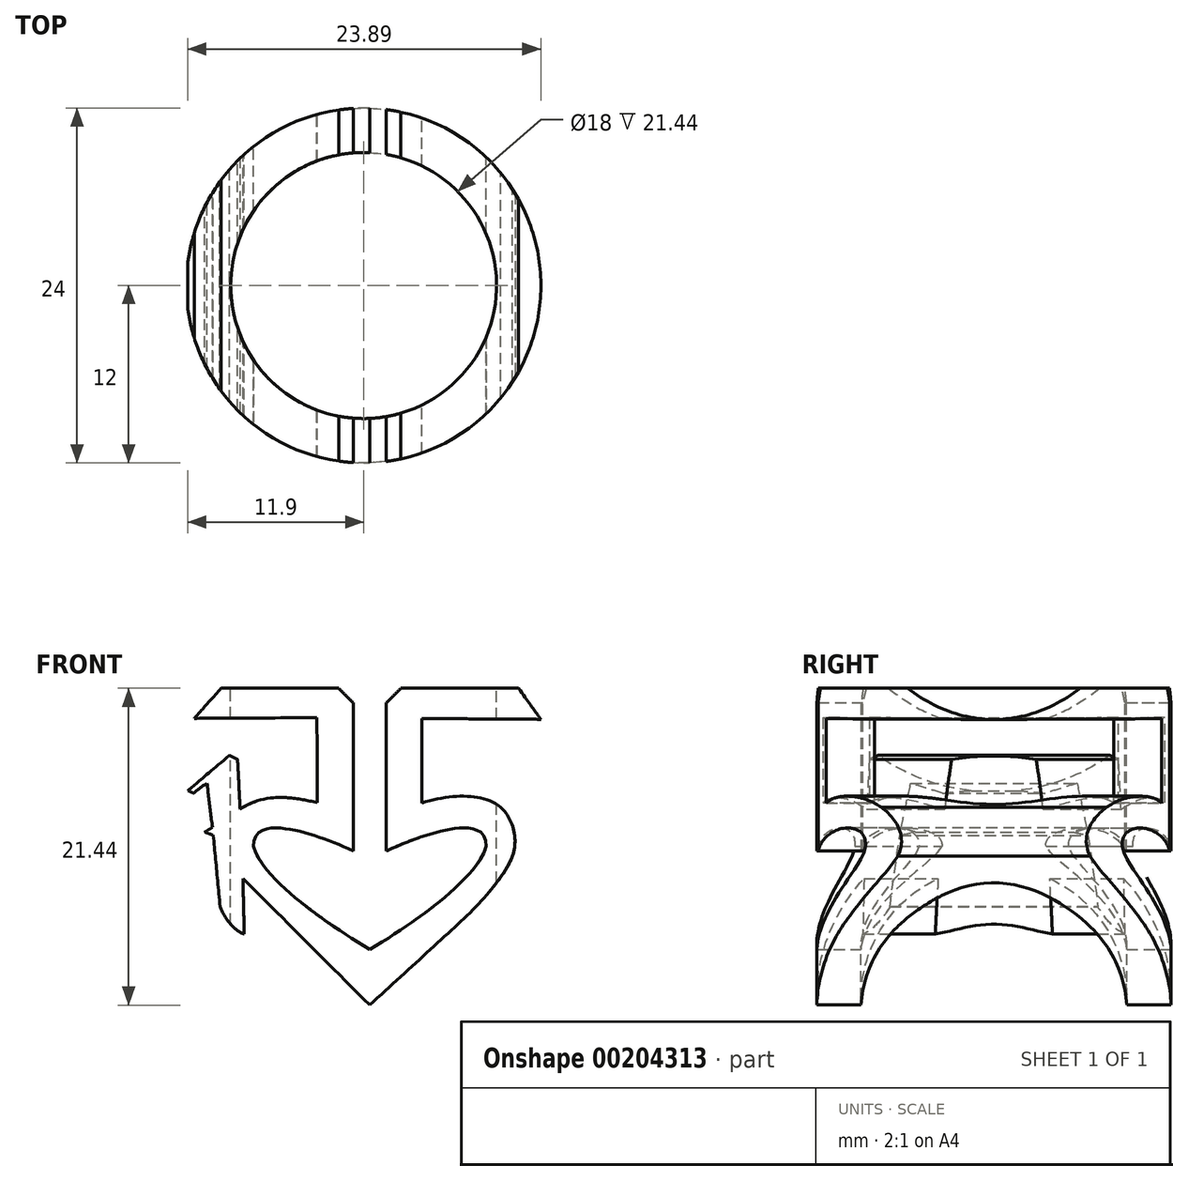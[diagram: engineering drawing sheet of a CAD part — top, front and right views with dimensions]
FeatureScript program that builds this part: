
annotation { "Feature Type Name" : "Feature", "Feature Type Description" : "" }
export const myFeature = defineFeature(function(context is Context, id is Id, definition is map)
    precondition{}
    {
        {
            var Q0;
            Q0=qCreatedBy(makeId("Top.planeOp"),FACE);
            var sketch = newSketch(context, id + "F0", { "sketchPlane" : qUnion([Q0])});
            skCircle(sketch, "E0", {"center": v(0, 0) * mm, "radius": 9 * mm});
            skCircle(sketch, "E1.0", {"center": v(0, 0) * mm, "radius": 12 * mm});
            skPoint(sketch, "E2", {"position": v(-12, 0) * mm});
            skPoint(sketch, "E3", {"position": v(12, 0) * mm});
            skSolve(sketch);
        }
        {
            var Q0;
            Q0=makeQuery(id+"F0.imprint","IMPRINT",FACE,{"disambiguationData":[TD([[makeQuery(id+"F0.imprint","IMPRINT",EDGE,{"derivedFrom":sQuery(id+"F0.wireOp",EDGE,"E0")}),-1.0]])]});
            extrude(context, id + "F1", {"entities" : qUnion([Q0]), "oppositeDirection" : true, "depth" : 26.1 * mm});
        }
        {
            var Q0;
            Q0=qCreatedBy(makeId("Front.planeOp"),FACE);
            var sketch = newSketch(context, id + "F2", { "sketchPlane" : qUnion([Q0])});
            skLineSegment(sketch, "E4.0", {"start": v(-15.68, 5) * mm, "end": v(-15.68, -16.21) * mm});
            skLineSegment(sketch, "E4.1", {"start": v(-15.68, -26.77) * mm, "end": v(15.68, -26.77) * mm});
            skLineSegment(sketch, "E4.2", {"start": v(15.68, -26.77) * mm, "end": v(15.68, -16.21) * mm});
            skLineSegment(sketch, "E4.3", {"start": v(-15.68, -16.21) * mm, "end": v(-15.68, -26.77) * mm});
            skLineSegment(sketch, "E4.4", {"start": v(15.68, 5) * mm, "end": v(15.68, -16.21) * mm});
            skLineSegment(sketch, "E4.5", {"start": v(15.68, 5) * mm, "end": v(-15.68, 5) * mm});
            skLineSegment(sketch, "E5", {"start": v(12, -3.2) * mm, "end": v(10.47, -1.1) * mm});
            skLineSegment(sketch, "E6", {"start": v(10.47, -1.1) * mm, "end": v(2.52, -1.1) * mm});
            skLineSegment(sketch, "E7", {"start": v(2.52, -1.1) * mm, "end": v(1.54, -2.09) * mm});
            skLineSegment(sketch, "E8", {"start": v(1.54, -2.09) * mm, "end": v(1.54, -12.1) * mm});
            skFitSpline(sketch, "E9", {"points": [v(0.42, -18.78) * mm, v(-7.44, -11.8) * mm], "startDerivative": vector(-11.84, 7.14) * mm, "endDerivative": vector(-1.22, 5.47) * mm});
            skFitSpline(sketch, "E10", {"points": [v(-7.44, -11.8) * mm, v(-0.7, -12.1) * mm], "startDerivative": vector(-0.48, 8.4) * mm, "endDerivative": vector(2.37, -1.11) * mm});
            skLineSegment(sketch, "E11", {"start": v(-0.7, -12.1) * mm, "end": v(-0.7, -2.09) * mm});
            skLineSegment(sketch, "E12.MirrorCS", {"start": v(-1.69, -1.1) * mm, "end": v(-0.7, -2.09) * mm});
            skLineSegment(sketch, "E13.MirrorCS", {"start": v(-9.64, -1.1) * mm, "end": v(-1.69, -1.1) * mm});
            skLineSegment(sketch, "E14", {"start": v(-9.64, -1.1) * mm, "end": v(-11.47, -3.14) * mm});
            skLineSegment(sketch, "E15", {"start": v(-11.47, -3.14) * mm, "end": v(-3.16, -3.09) * mm});
            skLineSegment(sketch, "E16", {"start": v(-3.16, -3.09) * mm, "end": v(-3.13, -8.84) * mm});
            skLineSegment(sketch, "E17", {"start": v(12, -3.2) * mm, "end": v(3.93, -3.15) * mm});
            skLineSegment(sketch, "E18", {"start": v(3.93, -3.15) * mm, "end": v(3.93, -8.86) * mm});
            skFitSpline(sketch, "E19", {"points": [v(3.93, -8.86) * mm, v(9.27, -9.16) * mm], "startDerivative": vector(5.06, 1.58) * mm, "endDerivative": vector(3.87, -3.25) * mm});
            skFitSpline(sketch, "E20", {"points": [v(9.27, -9.16) * mm, v(10.08, -12.46) * mm], "startDerivative": vector(2.58, -2.38) * mm, "endDerivative": vector(-1.17, -3.7) * mm});
            skPoint(sketch, "E21", {"position": v(6.16, -17.29) * mm});
            skFitSpline(sketch, "E22", {"points": [v(6.16, -17.27) * mm, v(10.08, -12.46) * mm], "startDerivative": vector(2.98, 2.71) * mm, "endDerivative": vector(2.23, 5.47) * mm});
            skLineSegment(sketch, "E23", {"start": v(6.16, -17.27) * mm, "end": v(0.4, -22.54) * mm});
            skLineSegment(sketch, "E24", {"start": v(0.4, -22.54) * mm, "end": v(-8.17, -13.97) * mm});
            skLineSegment(sketch, "E25", {"start": v(-8.17, -13.97) * mm, "end": v(-8.08, -17.73) * mm});
            skFitSpline(sketch, "E26", {"points": [v(-8.08, -17.73) * mm, v(-9.72, -15.87) * mm], "startDerivative": vector(-3.5, 1.22) * mm, "endDerivative": vector(0.33, -0.8) * mm});
            skLineSegment(sketch, "E27", {"start": v(-9.72, -15.87) * mm, "end": v(-10.18, -11.05) * mm});
            skLineSegment(sketch, "E28", {"start": v(-10.18, -11.05) * mm, "end": v(-10.75, -10.83) * mm});
            skLineSegment(sketch, "E29", {"start": v(-10.75, -10.83) * mm, "end": v(-10.23, -10.51) * mm});
            skLineSegment(sketch, "E30", {"start": v(-10.23, -10.51) * mm, "end": v(-10.6, -7.55) * mm});
            skFitSpline(sketch, "E31", {"points": [v(-10.6, -7.55) * mm, v(-11.48, -8.2) * mm], "startDerivative": vector(-1.38, -0.68) * mm, "endDerivative": vector(-0.49, -0.5) * mm});
            skLineSegment(sketch, "E32", {"start": v(-11.48, -8.2) * mm, "end": v(-11.9, -8.03) * mm});
            skLineSegment(sketch, "E33", {"start": v(-11.9, -8.03) * mm, "end": v(-9.1, -5.64) * mm});
            skLineSegment(sketch, "E34", {"start": v(-9.1, -5.64) * mm, "end": v(-8.53, -5.92) * mm});
            skLineSegment(sketch, "E35", {"start": v(-8.53, -5.92) * mm, "end": v(-8.36, -9.27) * mm});
            skFitSpline(sketch, "E36", {"points": [v(-8.36, -9.27) * mm, v(-3.13, -8.84) * mm], "startDerivative": vector(2.72, 1.6) * mm, "endDerivative": vector(9.49, -2.31) * mm});
            skFitSpline(sketch, "E37.MirrorCS", {"points": [v(8.28, -11.8) * mm, v(1.54, -12.1) * mm], "startDerivative": vector(0.48, 8.4) * mm, "endDerivative": vector(-2.37, -1.11) * mm});
            skFitSpline(sketch, "E38.MirrorCS", {"points": [v(0.42, -18.78) * mm, v(8.28, -11.8) * mm], "startDerivative": vector(11.84, 7.14) * mm, "endDerivative": vector(1.22, 5.47) * mm});
            skLineSegment(sketch, "E39.MirrorCS", {"start": v(1.54, -12.1) * mm, "end": v(1.54, -2.09) * mm});
            skSolve(sketch);
        }
        {
            var Q0;
            Q0 = qSketchRegion(id + "F2", true);
            extrude(context, id + "F3", {"entities" : qUnion([Q0]), "operationType" : NewBodyOperationType.REMOVE, "endBound" : BoundingType.SYMMETRIC, "depth" : 42.6 * mm});
        }
    });
